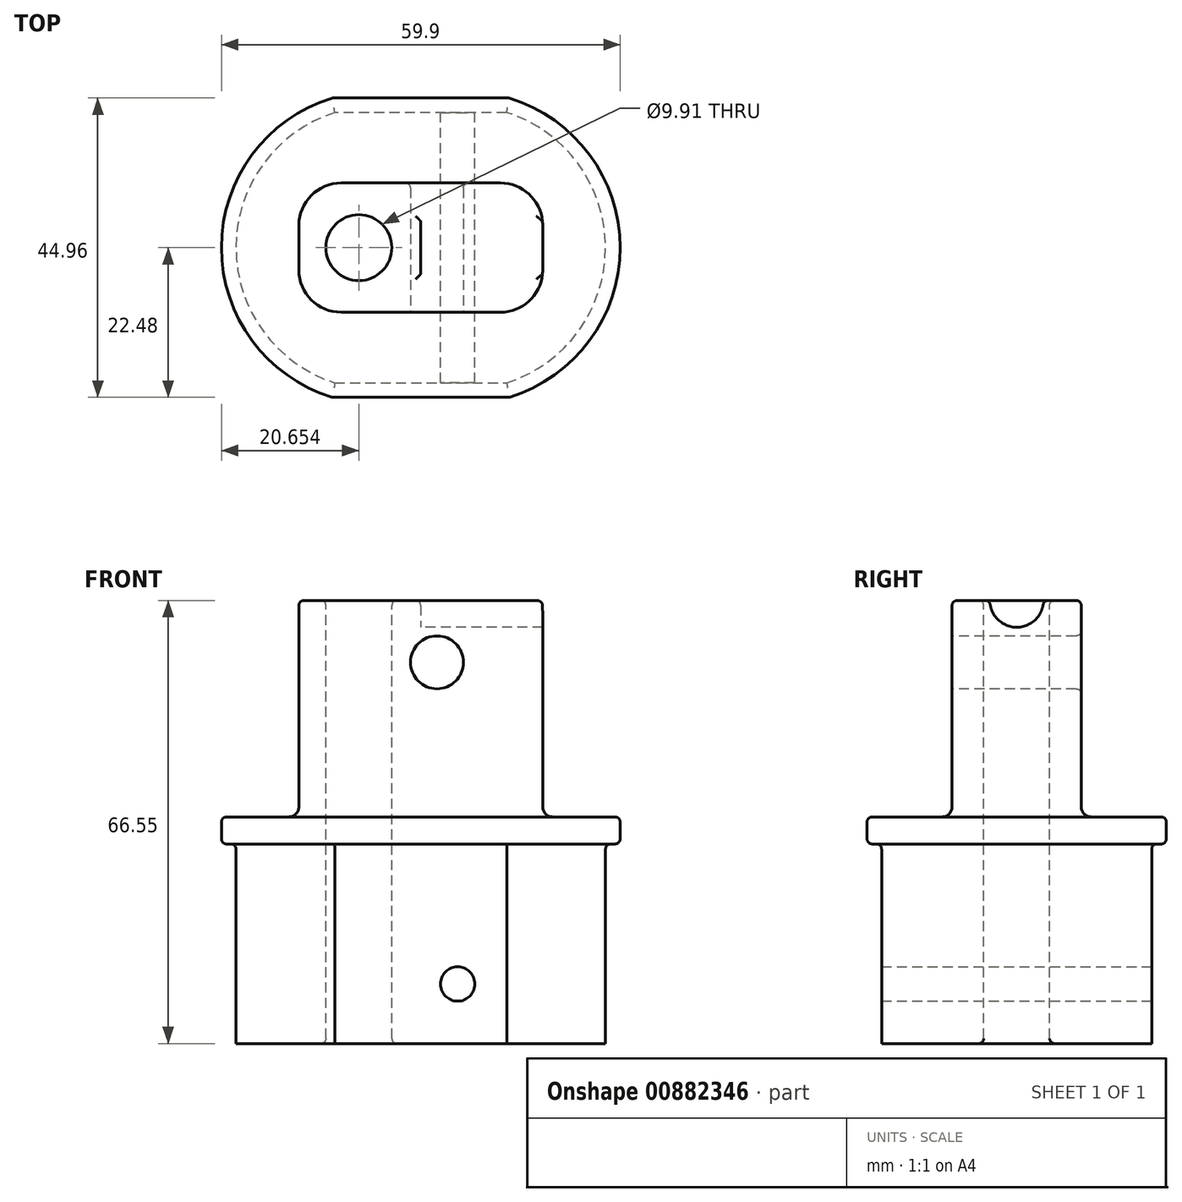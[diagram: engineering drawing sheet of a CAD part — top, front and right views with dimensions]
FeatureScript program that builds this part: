
annotation { "Feature Type Name" : "Feature", "Feature Type Description" : "" }
export const myFeature = defineFeature(function(context is Context, id is Id, definition is map)
    precondition{}
    {
        {
            var Q0;
            Q0=qCreatedBy(makeId("Top.planeOp"),FACE);
            var sketch = newSketch(context, id + "F0", { "sketchPlane" : qUnion([Q0])});
            skArc(sketch, "E0", {"start": v(-13.25, 22.48) * mm, "mid": v(-29.95, 0) * mm, "end": v(-13.25, -22.48) * mm});
            skArc(sketch, "E1", {"start": v(13.25, -22.48) * mm, "mid": v(29.95, 0) * mm, "end": v(13.25, 22.48) * mm});
            skLineSegment(sketch, "E2", {"start": v(-13.25, -22.48) * mm, "end": v(13.25, -22.48) * mm});
            skLineSegment(sketch, "E3", {"start": v(13.25, 22.48) * mm, "end": v(-13.25, 22.48) * mm});
            skLineSegment(sketch, "E4", {"start": v(0, 22.48) * mm, "end": v(0, 0) * mm, "construction": true});
            skLineSegment(sketch, "E5", {"start": v(0, 0) * mm, "end": v(0, -22.48) * mm, "construction": true});
            skLineSegment(sketch, "E6", {"start": v(0, 0) * mm, "end": v(-6.47, 0) * mm, "construction": true});
            skLineSegment(sketch, "E7", {"start": v(0, 0) * mm, "end": v(6.47, 0) * mm, "construction": true});
            skSolve(sketch);
        }
        {
            var Q0;
            Q0 = qSketchRegion(id + "F0", true);
            extrude(context, id + "F1", {"entities" : qUnion([Q0]), "depth" : 66.55 * mm, "offsetDistance" : 25.4 * mm});
        }
        {
            var Q0;
            Q0=makeQuery(id+"F1.opExtrude","CAP_FACE",FACE,{"disambiguationData":[OSD([sQuery(id+"F0.wireOp",EDGE,"E0"),sQuery(id+"F0.wireOp",EDGE,"E1"),sQuery(id+"F0.wireOp",EDGE,"E2"),sQuery(id+"F0.wireOp",EDGE,"E3")])],"isStart":false});
            var sketch = newSketch(context, id + "F2", { "sketchPlane" : qUnion([Q0])});
            skSolve(sketch);
        }
        {
            var Q0;
            Q0=makeQuery(id+"F1.opExtrude","CAP_FACE",FACE,{"disambiguationData":[OSD([sQuery(id+"F0.wireOp",EDGE,"E0"),sQuery(id+"F0.wireOp",EDGE,"E1"),sQuery(id+"F0.wireOp",EDGE,"E2"),sQuery(id+"F0.wireOp",EDGE,"E3")])],"isStart":true});
            var sketch = newSketch(context, id + "F3", { "sketchPlane" : qUnion([Q0])});
            skLineSegment(sketch, "E8.0", {"start": v(-12.92, 20.3) * mm, "end": v(12.92, 20.3) * mm});
            skArc(sketch, "E8.1", {"start": v(-12.92, -20.3) * mm, "mid": v(-27.76, 0) * mm, "end": v(-12.92, 20.3) * mm});
            skLineSegment(sketch, "E8.2", {"start": v(12.92, -20.3) * mm, "end": v(-12.92, -20.3) * mm});
            skArc(sketch, "E8.3", {"start": v(12.92, 20.3) * mm, "mid": v(27.76, 0) * mm, "end": v(12.92, -20.3) * mm});
            skArc(sketch, "E9.0", {"start": v(13.25, 22.48) * mm, "mid": v(29.95, 0) * mm, "end": v(13.25, -22.48) * mm});
            skLineSegment(sketch, "E10.0", {"start": v(13.25, -22.48) * mm, "end": v(-13.25, -22.48) * mm});
            skArc(sketch, "E10.1", {"start": v(-13.25, -22.48) * mm, "mid": v(-29.95, 0) * mm, "end": v(-13.25, 22.48) * mm});
            skLineSegment(sketch, "E10.2", {"start": v(-13.25, 22.48) * mm, "end": v(13.25, 22.48) * mm});
            skSolve(sketch);
        }
        {
            var Q0;
            Q0 = qSketchRegion(id + "F3", true);
            extrude(context, id + "F4", {"entities" : qUnion([Q0]), "operationType" : NewBodyOperationType.REMOVE, "oppositeDirection" : true, "depth" : 29.97 * mm, "offsetDistance" : 25.4 * mm});
        }
        {
            var Q0;
            Q0=makeQuery(id+"F2.imprint","IMPRINT",FACE,{"disambiguationData":[TD([[makeQuery(id+"F2.imprint","IMPRINT",EDGE,{"derivedFrom":makeQuery(id+"F1.opExtrude","CAP_EDGE",EDGE,{"disambiguationData":[OSD([sQuery(id+"F0.wireOp",EDGE,"E0")])],"isStart":false})}),1.0]])]});
            var sketch = newSketch(context, id + "F5", { "sketchPlane" : qUnion([Q0])});
            skArc(sketch, "E11.0.0", {"start": v(-13.25, 22.48) * mm, "mid": v(-29.95, 0) * mm, "end": v(-13.25, -22.48) * mm});
            skLineSegment(sketch, "E11.0.1", {"start": v(-13.25, -22.48) * mm, "end": v(13.25, -22.48) * mm});
            skArc(sketch, "E11.0.2", {"start": v(13.25, -22.48) * mm, "mid": v(29.95, 0) * mm, "end": v(13.25, 22.48) * mm});
            skLineSegment(sketch, "E11.0.3", {"start": v(13.25, 22.48) * mm, "end": v(-13.25, 22.48) * mm});
            skLineSegment(sketch, "E12.1", {"start": v(11.96, 9.7) * mm, "end": v(-11.96, 9.7) * mm});
            skLineSegment(sketch, "E12.3", {"start": v(-11.96, -9.7) * mm, "end": v(11.96, -9.7) * mm});
            skLineSegment(sketch, "E13", {"start": v(-18.31, 3.35) * mm, "end": v(-18.31, -3.35) * mm});
            skLineSegment(sketch, "E14", {"start": v(18.31, 3.35) * mm, "end": v(18.31, -3.35) * mm});
            skPoint(sketch, "E15.visualSharp", {"position": v(18.31, 9.7) * mm});
            skArc(sketch, "E15.filletArc", {"start": v(18.31, 3.35) * mm, "mid": v(16.45, 7.84) * mm, "end": v(11.96, 9.7) * mm});
            skPoint(sketch, "E16.visualSharp", {"position": v(18.31, -9.7) * mm});
            skArc(sketch, "E16.filletArc", {"start": v(11.96, -9.7) * mm, "mid": v(16.45, -7.84) * mm, "end": v(18.31, -3.35) * mm});
            skPoint(sketch, "E17.visualSharp", {"position": v(-18.31, -9.7) * mm});
            skArc(sketch, "E17.filletArc", {"start": v(-18.31, -3.35) * mm, "mid": v(-16.45, -7.84) * mm, "end": v(-11.96, -9.7) * mm});
            skPoint(sketch, "E18.visualSharp", {"position": v(-18.31, 9.7) * mm});
            skArc(sketch, "E18.filletArc", {"start": v(-11.96, 9.7) * mm, "mid": v(-16.45, 7.84) * mm, "end": v(-18.31, 3.35) * mm});
            skSolve(sketch);
        }
        {
            var Q0;
            Q0 = qSketchRegion(id + "F5", true);
            extrude(context, id + "F6", {"entities" : qUnion([Q0]), "operationType" : NewBodyOperationType.REMOVE, "oppositeDirection" : true, "depth" : 32.5 * mm, "offsetDistance" : 25.4 * mm});
        }
        {
            var Q0;
            Q0=makeQuery(id+"F4.boolean.opBoolean","COPY",FACE,{"derivedFrom":makeQuery(id+"F4.opExtrude","SWEPT_FACE",FACE,{"disambiguationData":[OSD([sQuery(id+"F3.wireOp",EDGE,"E8.2")])]})});
            var sketch = newSketch(context, id + "F7", { "sketchPlane" : qUnion([Q0])});
            skPoint(sketch, "E19", {"position": v(-5.54, 8.94) * mm});
            skPoint(sketch, "E19.positionSnap0", {"position": v(0, 29.97) * mm});
            skSolve(sketch);
        }
        {
            var Q0;
            Q0=sQuery(id+"F7.wireOp",VERTEX,"E19");
            var Q1;
            Q1=makeQuery(id+"F1.opExtrude","SWEPT_BODY",BODY,{"disambiguationData":[OSD([sQuery(id+"F0.wireOp",EDGE,"E0"),sQuery(id+"F0.wireOp",EDGE,"E1"),sQuery(id+"F0.wireOp",EDGE,"E2"),sQuery(id+"F0.wireOp",EDGE,"E3")])]});
            hole(context, id + "F8", {"style" : HoleStyle.SIMPLE, "endStyle" : HoleEndStyle.THROUGH, "holeDiameter" : 5.16 * mm, "majorDiameter" : 6.35 * mm, "isTappedThrough" : true, "tappedDepth" : 12.7 * mm, "tapClearance" : 3, "startFromSketch" : true, "locations" : qUnion([Q0]), "scope" : qUnion([Q1])});
        }
        {
            var Q0;
            Q0=makeQuery(id+"F6.boolean.opBoolean","COPY",FACE,{"derivedFrom":makeQuery(id+"F6.opExtrude","SWEPT_FACE",FACE,{"disambiguationData":[OSD([sQuery(id+"F5.wireOp",EDGE,"E12.3")])]})});
            var sketch = newSketch(context, id + "F9", { "sketchPlane" : qUnion([Q0])});
            skCircle(sketch, "E20", {"center": v(2.44, 57.25) * mm, "radius": 3.97 * mm});
            skSolve(sketch);
        }
        {
            var Q0;
            Q0 = qSketchRegion(id + "F9", true);
            extrude(context, id + "F10", {"entities" : qUnion([Q0]), "operationType" : NewBodyOperationType.REMOVE, "endBound" : BoundingType.THROUGH_ALL, "oppositeDirection" : true, "depth" : 25.4 * mm, "offsetDistance" : 25.4 * mm});
        }
        {
            var Q0;
            Q0=qCreatedBy(makeId("Right.planeOp"),FACE);
            var sketch = newSketch(context, id + "F11", { "sketchPlane" : qUnion([Q0])});
            skCircle(sketch, "E21", {"center": v(0, 66.55) * mm, "radius": 4.03 * mm});
            skSolve(sketch);
        }
        {
            var Q0;
            Q0 = qSketchRegion(id + "F11", true);
            extrude(context, id + "F12", {"entities" : qUnion([Q0]), "operationType" : NewBodyOperationType.REMOVE, "endBound" : BoundingType.THROUGH_ALL, "depth" : 25.4 * mm, "offsetDistance" : 25.4 * mm});
        }
        {
            var Q0;
            Q0=makeQuery(id+"F2.imprint","IMPRINT",FACE,{"disambiguationData":[TD([[makeQuery(id+"F2.imprint","IMPRINT",EDGE,{"derivedFrom":makeQuery(id+"F1.opExtrude","CAP_EDGE",EDGE,{"disambiguationData":[OSD([sQuery(id+"F0.wireOp",EDGE,"E0")])],"isStart":false})}),1.0]])]});
            var sketch = newSketch(context, id + "F13", { "sketchPlane" : qUnion([Q0])});
            skCircle(sketch, "E22", {"center": v(-9.3, 0) * mm, "radius": 4.95 * mm});
            skSolve(sketch);
        }
        {
            var Q0;
            Q0 = qSketchRegion(id + "F13", true);
            extrude(context, id + "F14", {"entities" : qUnion([Q0]), "operationType" : NewBodyOperationType.REMOVE, "endBound" : BoundingType.THROUGH_ALL, "oppositeDirection" : true, "depth" : 25.4 * mm, "offsetDistance" : 25.4 * mm});
        }
        {
            var Q0;
            Q0=makeQuery(id+"F6.boolean.opBoolean","COPY",EDGE,{"derivedFrom":makeQuery(id+"F6.opExtrude","CAP_EDGE",EDGE,{"disambiguationData":[OSD([sQuery(id+"F5.wireOp",EDGE,"E12.3")])],"isStart":false})});
            var Q1;
            Q1=makeQuery(id+"F6.boolean.opBoolean","COPY",EDGE,{"derivedFrom":makeQuery(id+"F6.opExtrude","CAP_EDGE",EDGE,{"disambiguationData":[OSD([sQuery(id+"F5.wireOp",EDGE,"E12.2")])],"isStart":false})});
            var Q2;
            Q2=makeQuery(id+"F6.boolean.opBoolean","COPY",EDGE,{"derivedFrom":makeQuery(id+"F6.opExtrude","CAP_EDGE",EDGE,{"disambiguationData":[OSD([sQuery(id+"F5.wireOp",EDGE,"E12.0")])],"isStart":false})});
            var Q3;
            Q3=makeQuery(id+"F6.boolean.opBoolean","COPY",EDGE,{"derivedFrom":makeQuery(id+"F6.opExtrude","CAP_EDGE",EDGE,{"disambiguationData":[OSD([sQuery(id+"F5.wireOp",EDGE,"E12.1")])],"isStart":false})});
            fillet(context, id + "F15", {"entities" : qUnion([Q0, Q1, Q2, Q3]), "radius" : 1.52 * mm, "tangentPropagation" : true, "allowEdgeOverflow" : false});
        }
        {
            var Q0;
            Q0=makeQuery(id+"F1.opExtrude","CAP_FACE",FACE,{"disambiguationData":[OSD([sQuery(id+"F0.wireOp",EDGE,"E0"),sQuery(id+"F0.wireOp",EDGE,"E1"),sQuery(id+"F0.wireOp",EDGE,"E2"),sQuery(id+"F0.wireOp",EDGE,"E3")])],"isStart":false});
            var Q1;
            Q1=makeQuery(id+"F10.boolean.opBoolean","COPY",EDGE,{"derivedFrom":makeQuery(id+"F10.opExtrude","CAP_EDGE",EDGE,{"disambiguationData":[OSD([sQuery(id+"F9.wireOp",EDGE,"E20")])],"isStart":true})});
            var Q2;
            Q2=makeQuery(id+"F8.hole-0.boolean.opBoolean","INTERSECT",EDGE,{"derivedFrom":[makeQuery(id+"F4.boolean.opBoolean","COPY",FACE,{"derivedFrom":makeQuery(id+"F4.opExtrude","SWEPT_FACE",FACE,{"disambiguationData":[OSD([sQuery(id+"F3.wireOp",EDGE,"E8.0")])]})}),makeQuery(id+"F8.hole-0.opRevolve","SWEPT_FACE",FACE,{"disambiguationData":[OSD([sQuery(id+"F8.hole-0.sketch.wireOp",EDGE,"core_line_2")])]})]});
            var Q3;
            Q3=makeQuery(id+"F10.boolean.opBoolean","INTERSECT",EDGE,{"derivedFrom":[makeQuery(id+"F6.boolean.opBoolean","COPY",FACE,{"derivedFrom":makeQuery(id+"F6.opExtrude","SWEPT_FACE",FACE,{"disambiguationData":[OSD([sQuery(id+"F5.wireOp",EDGE,"E12.1")])]})}),makeQuery(id+"F10.opExtrude","SWEPT_FACE",FACE,{"disambiguationData":[OSD([sQuery(id+"F9.wireOp",EDGE,"E20")])]})]});
            var Q4;
            Q4=makeQuery(id+"F8.hole-0.boolean.opBoolean","COPY",EDGE,{"derivedFrom":makeQuery(id+"F8.hole-0.opRevolve","SWEPT_EDGE",EDGE,{"disambiguationData":[OSD([sQuery(id+"F8.hole-0.sketch.wireOp",EDGE,"core_line_2"),sQuery(id+"F8.hole-0.sketch.wireOp",EDGE,"core_line_3")])]})});
            var Q5;
            Q5=makeQuery(id+"F14.boolean.opBoolean","INTERSECT",EDGE,{"derivedFrom":[makeQuery(id+"F1.opExtrude","CAP_FACE",FACE,{"disambiguationData":[OSD([sQuery(id+"F0.wireOp",EDGE,"E0"),sQuery(id+"F0.wireOp",EDGE,"E1"),sQuery(id+"F0.wireOp",EDGE,"E2"),sQuery(id+"F0.wireOp",EDGE,"E3")])],"isStart":true}),makeQuery(id+"F14.opExtrude","SWEPT_FACE",FACE,{"disambiguationData":[OSD([sQuery(id+"F13.wireOp",EDGE,"E22")])]})]});
            var Q6;
            Q6=makeQuery(id+"F12.boolean.opBoolean","INTERSECT",EDGE,{"derivedFrom":[makeQuery(id+"F6.boolean.opBoolean","COPY",FACE,{"derivedFrom":makeQuery(id+"F6.opExtrude","SWEPT_FACE",FACE,{"disambiguationData":[OSD([sQuery(id+"F5.wireOp",EDGE,"E12.2")])]})}),makeQuery(id+"F12.opExtrude","SWEPT_FACE",FACE,{"disambiguationData":[OSD([sQuery(id+"F11.wireOp",EDGE,"E21")])]})]});
            fillet(context, id + "F16", {"entities" : qUnion([Q0, Q1, Q2, Q3, Q4, Q5, Q6]), "radius" : 0.76 * mm, "tangentPropagation" : true, "allowEdgeOverflow" : false});
        }
        {
            var Q0;
            Q0=makeQuery(id+"F4.boolean.opBoolean","COPY",EDGE,{"derivedFrom":makeQuery(id+"F4.opExtrude","CAP_EDGE",EDGE,{"disambiguationData":[OSD([sQuery(id+"F3.wireOp",EDGE,"E8.1")])],"isStart":false})});
            var Q1;
            Q1=makeQuery(id+"F4.boolean.opBoolean","COPY",EDGE,{"derivedFrom":makeQuery(id+"F4.opExtrude","CAP_EDGE",EDGE,{"disambiguationData":[OSD([sQuery(id+"F3.wireOp",EDGE,"E8.0")])],"isStart":false})});
            var Q2;
            Q2=makeQuery(id+"F4.boolean.opBoolean","COPY",EDGE,{"derivedFrom":makeQuery(id+"F4.opExtrude","CAP_EDGE",EDGE,{"disambiguationData":[OSD([sQuery(id+"F3.wireOp",EDGE,"E8.3")])],"isStart":false})});
            var Q3;
            Q3=makeQuery(id+"F4.boolean.opBoolean","COPY",EDGE,{"derivedFrom":makeQuery(id+"F4.opExtrude","CAP_EDGE",EDGE,{"disambiguationData":[OSD([sQuery(id+"F3.wireOp",EDGE,"E8.2")])],"isStart":false})});
            var Q4;
            Q4=makeQuery(id+"F4.boolean.opBoolean","COPY",EDGE,{"derivedFrom":makeQuery(id+"F4.opExtrude","CAP_EDGE",EDGE,{"disambiguationData":[OSD([sQuery(id+"F3.wireOp",EDGE,"E8.3")])],"isStart":true})});
            var Q5;
            Q5=makeQuery(id+"F4.boolean.opBoolean","COPY",EDGE,{"derivedFrom":makeQuery(id+"F4.opExtrude","CAP_EDGE",EDGE,{"disambiguationData":[OSD([sQuery(id+"F3.wireOp",EDGE,"E8.2")])],"isStart":true})});
            var Q6;
            Q6=makeQuery(id+"F4.boolean.opBoolean","COPY",EDGE,{"derivedFrom":makeQuery(id+"F4.opExtrude","CAP_EDGE",EDGE,{"disambiguationData":[OSD([sQuery(id+"F3.wireOp",EDGE,"E8.0")])],"isStart":true})});
            var Q7;
            Q7=makeQuery(id+"F4.boolean.opBoolean","COPY",EDGE,{"derivedFrom":makeQuery(id+"F4.opExtrude","CAP_EDGE",EDGE,{"disambiguationData":[OSD([sQuery(id+"F3.wireOp",EDGE,"E8.1")])],"isStart":true})});
            fillet(context, id + "F17", {"entities" : qUnion([Q0, Q1, Q2, Q3, Q4, Q5, Q6, Q7]), "radius" : 0.76 * mm, "tangentPropagation" : true, "allowEdgeOverflow" : false});
        }
        {
            var Q0;
            Q0=makeQuery(id+"F1.opExtrude","SWEPT_FACE",FACE,{"disambiguationData":[OSD([sQuery(id+"F0.wireOp",EDGE,"E1")])]});
            var Q1;
            Q1=makeQuery(id+"F1.opExtrude","SWEPT_FACE",FACE,{"disambiguationData":[OSD([sQuery(id+"F0.wireOp",EDGE,"E2")])]});
            var Q2;
            Q2=makeQuery(id+"F1.opExtrude","SWEPT_FACE",FACE,{"disambiguationData":[OSD([sQuery(id+"F0.wireOp",EDGE,"E0")])]});
            var Q3;
            Q3=makeQuery(id+"F1.opExtrude","SWEPT_FACE",FACE,{"disambiguationData":[OSD([sQuery(id+"F0.wireOp",EDGE,"E3")])]});
            fillet(context, id + "F18", {"entities" : qUnion([Q0, Q1, Q2, Q3]), "radius" : 0.76 * mm, "tangentPropagation" : true, "allowEdgeOverflow" : false});
        }
    });
